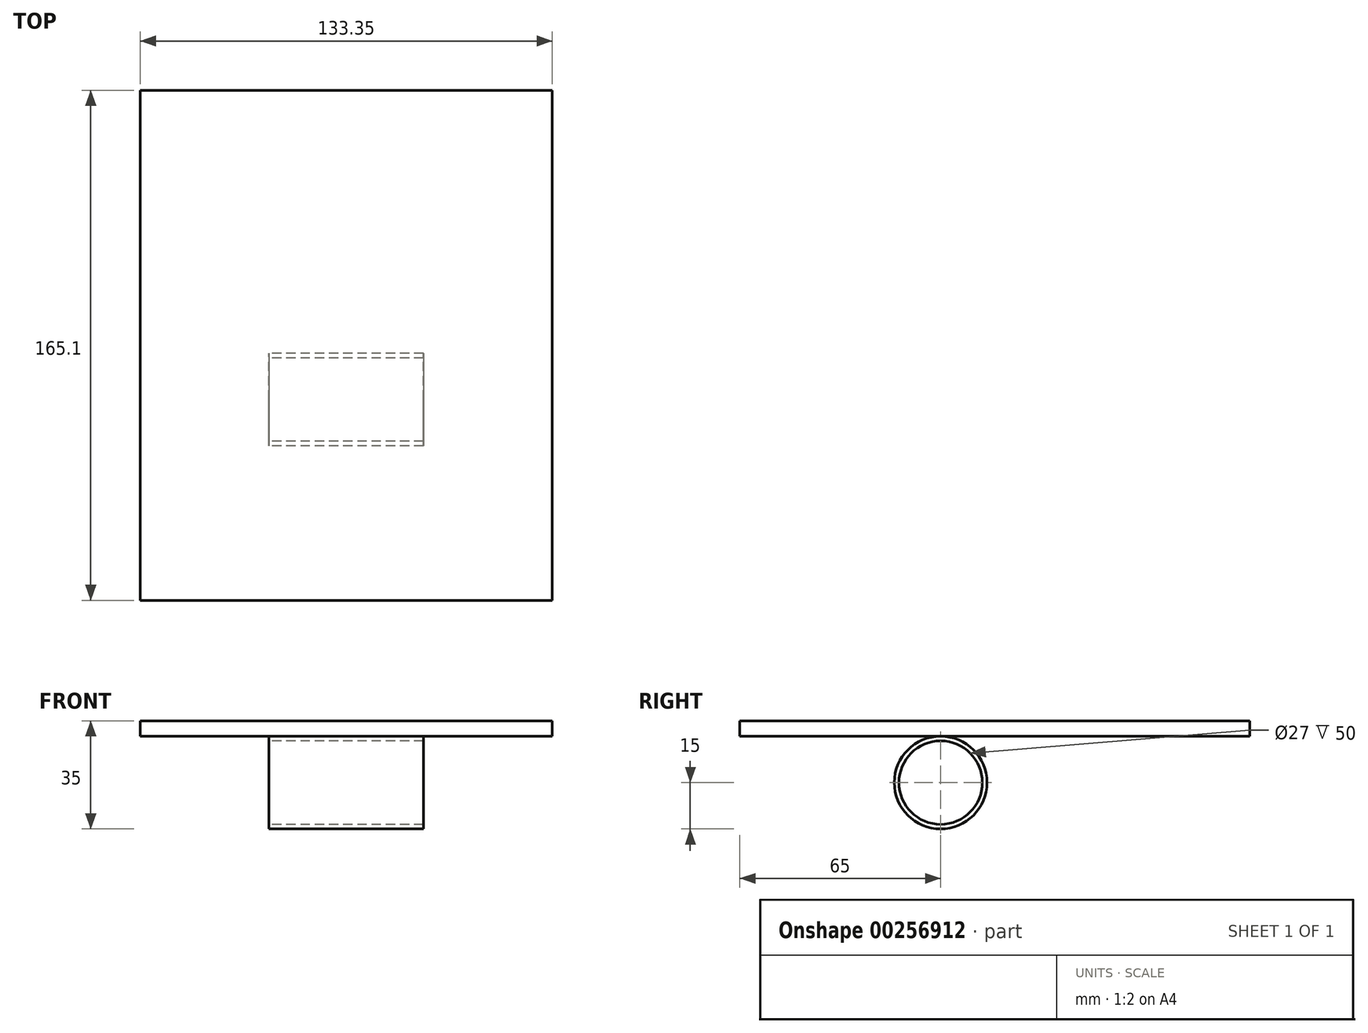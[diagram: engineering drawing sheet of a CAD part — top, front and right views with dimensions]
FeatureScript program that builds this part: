
annotation { "Feature Type Name" : "Feature", "Feature Type Description" : "" }
export const myFeature = defineFeature(function(context is Context, id is Id, definition is map)
    precondition{}
    {
        {
            var Q0;
            Q0=qCreatedBy(makeId("Top.planeOp"),FACE);
            var sketch = newSketch(context, id + "F0", { "sketchPlane" : qUnion([Q0])});
            skLineSegment(sketch, "E0.bottom", {"start": v(0, 0) * mm, "end": v(-133.35, 0) * mm});
            skLineSegment(sketch, "E0.top", {"start": v(0, 165.1) * mm, "end": v(-133.35, 165.1) * mm});
            skLineSegment(sketch, "E0.left", {"start": v(0, 0) * mm, "end": v(0, 165.1) * mm});
            skLineSegment(sketch, "E0.right", {"start": v(-133.35, 0) * mm, "end": v(-133.35, 165.1) * mm});
            skSolve(sketch);
        }
        {
            var Q0;
            Q0=makeQuery(id+"F0.imprint","IMPRINT",FACE,{"disambiguationData":[TD([[makeQuery(id+"F0.imprint","IMPRINT",EDGE,{"derivedFrom":sQuery(id+"F0.wireOp",EDGE,"E0.bottom")}),-1.0]])]});
            extrude(context, id + "F1", {"entities" : qUnion([Q0]), "depth" : 5 * mm});
        }
        {
            var Q0;
            Q0=makeQuery(id+"F1.opExtrude","SWEPT_FACE",FACE,{"disambiguationData":[OSD([sQuery(id+"F0.wireOp",EDGE,"E0.left")])]});
            var Q1;
            Q1=makeQuery(id+"F1.opExtrude","SWEPT_FACE",FACE,{"disambiguationData":[OSD([sQuery(id+"F0.wireOp",EDGE,"E0.right")])]});
            cPlane(context, id + "F2", {"entities" : qUnion([Q0, Q1]), "cplaneType" : CPlaneType.MID_PLANE, "offset" : 25.4 * mm, "width" : 152.4 * mm, "height" : 152.4 * mm});
        }
        {
            var Q0;
            Q0=qCreatedBy(id+"F2.planeOp",FACE);
            var sketch = newSketch(context, id + "F3", { "sketchPlane" : qUnion([Q0])});
            skCircle(sketch, "E1", {"center": v(65, -15) * mm, "radius": 15 * mm});
            skCircle(sketch, "E2", {"center": v(65, -15) * mm, "radius": 13.5 * mm});
            skSolve(sketch);
        }
        {
            var Q0;
            Q0=makeQuery(id+"F3.imprint","IMPRINT",FACE,{"disambiguationData":[TD([[makeQuery(id+"F3.imprint","IMPRINT",EDGE,{"derivedFrom":sQuery(id+"F3.wireOp",EDGE,"E1")}),1.0]])]});
            extrude(context, id + "F4", {"entities" : qUnion([Q0]), "endBound" : BoundingType.SYMMETRIC, "depth" : 50 * mm});
        }
    });
